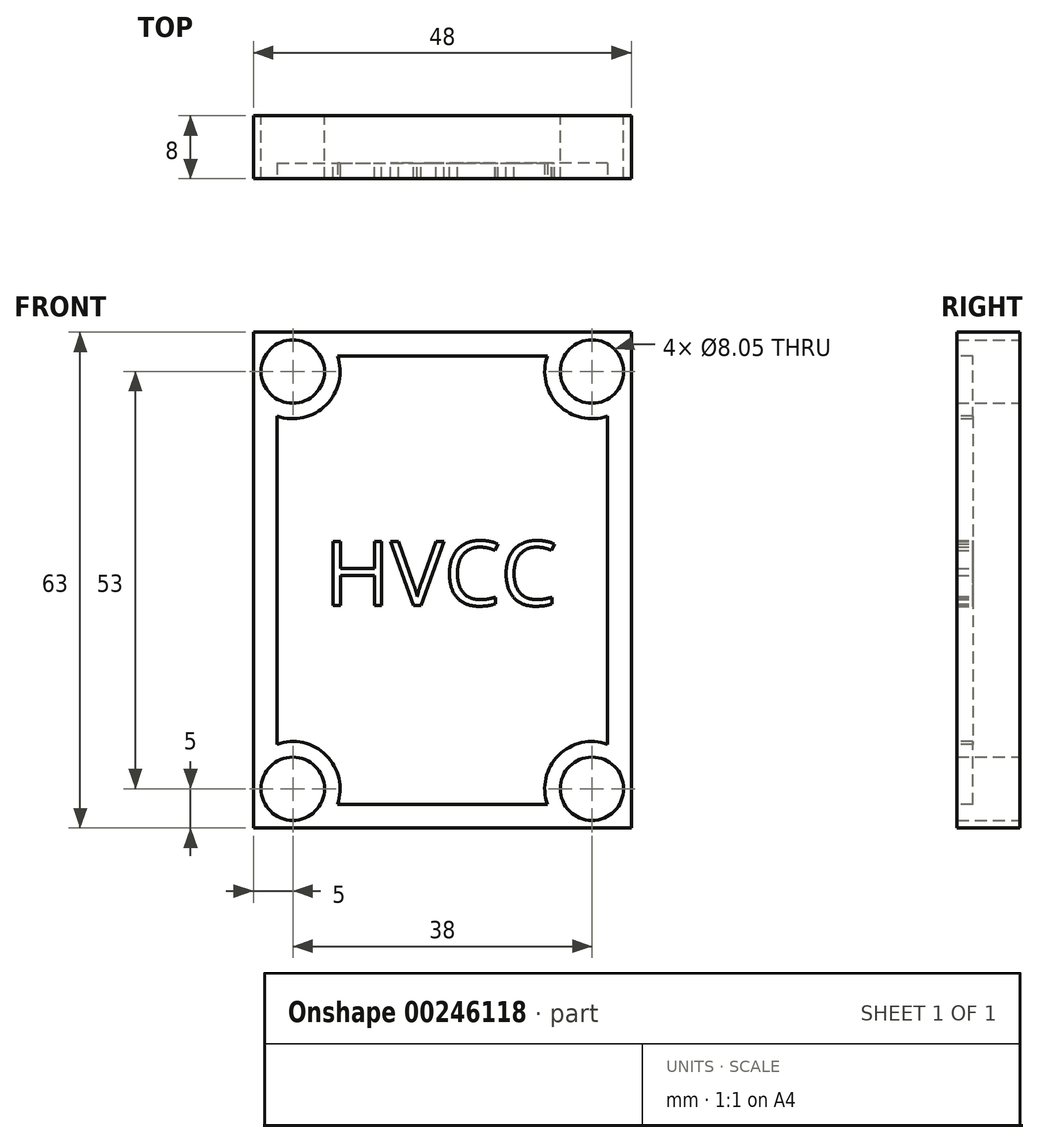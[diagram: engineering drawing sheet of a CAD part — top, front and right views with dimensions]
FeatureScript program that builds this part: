
annotation { "Feature Type Name" : "Feature", "Feature Type Description" : "" }
export const myFeature = defineFeature(function(context is Context, id is Id, definition is map)
    precondition{}
    {
        {
            var Q0;
            Q0=qCreatedBy(makeId("Front.planeOp"),FACE);
            var sketch = newSketch(context, id + "F0", { "sketchPlane" : qUnion([Q0])});
            skLineSegment(sketch, "E0.bottom", {"start": v(0, 0) * mm, "end": v(-48, 0) * mm});
            skLineSegment(sketch, "E0.top", {"start": v(0, -63) * mm, "end": v(-48, -63) * mm});
            skLineSegment(sketch, "E0.left", {"start": v(0, 0) * mm, "end": v(0, -63) * mm});
            skLineSegment(sketch, "E0.right", {"start": v(-48, 0) * mm, "end": v(-48, -63) * mm});
            skCircle(sketch, "E1", {"center": v(-43, -5) * mm, "radius": 4.03 * mm});
            skCircle(sketch, "E2", {"center": v(-5, -5) * mm, "radius": 4.03 * mm});
            skCircle(sketch, "E3", {"center": v(-43, -58) * mm, "radius": 4.03 * mm});
            skCircle(sketch, "E4", {"center": v(-5, -58) * mm, "radius": 4.03 * mm});
            skLineSegment(sketch, "E5", {"start": v(-45, -13) * mm, "end": v(-45, -50) * mm});
            skLineSegment(sketch, "E6", {"start": v(-43, -52) * mm, "end": v(-43, -52) * mm});
            skLineSegment(sketch, "E7", {"start": v(-37, -58) * mm, "end": v(-37, -58) * mm});
            skLineSegment(sketch, "E8", {"start": v(-35, -60) * mm, "end": v(-13, -60) * mm});
            skLineSegment(sketch, "E9", {"start": v(-11, -58) * mm, "end": v(-11, -58) * mm});
            skLineSegment(sketch, "E10", {"start": v(-5, -52) * mm, "end": v(-5, -52) * mm});
            skLineSegment(sketch, "E11", {"start": v(-3, -50) * mm, "end": v(-3, -13) * mm});
            skLineSegment(sketch, "E12", {"start": v(-5, -11) * mm, "end": v(-5, -11) * mm});
            skLineSegment(sketch, "E13", {"start": v(-11, -5) * mm, "end": v(-11, -5) * mm});
            skLineSegment(sketch, "E14", {"start": v(-13, -3) * mm, "end": v(-35, -3) * mm});
            skLineSegment(sketch, "E15", {"start": v(-37, -5) * mm, "end": v(-37, -5) * mm});
            skLineSegment(sketch, "E16", {"start": v(-43, -11) * mm, "end": v(-43, -11) * mm});
            skLineSegment(sketch, "E17", {"start": v(-24, 0) * mm, "end": v(-24, -63) * mm, "construction": true});
            skLineSegment(sketch, "E18", {"start": v(-48, -31.5) * mm, "end": v(0, -31.5) * mm, "construction": true});
            skPoint(sketch, "E19.visualSharp", {"position": v(-37, -11) * mm});
            skArc(sketch, "E20.filletArc", {"start": v(-43, -11) * mm, "mid": v(-38.76, -9.24) * mm, "end": v(-37, -5) * mm});
            skPoint(sketch, "E21.visualSharp", {"position": v(-37, -3) * mm});
            skArc(sketch, "E21.filletArc", {"start": v(-35, -3) * mm, "mid": v(-36.41, -3.59) * mm, "end": v(-37, -5) * mm});
            skPoint(sketch, "E22.visualSharp", {"position": v(-45, -11) * mm});
            skArc(sketch, "E22.filletArc", {"start": v(-43, -11) * mm, "mid": v(-44.41, -11.59) * mm, "end": v(-45, -13) * mm});
            skPoint(sketch, "E23.visualSharp", {"position": v(-11, -11) * mm});
            skArc(sketch, "E23.filletArc", {"start": v(-11, -5) * mm, "mid": v(-9.24, -9.24) * mm, "end": v(-5, -11) * mm});
            skPoint(sketch, "E24.visualSharp", {"position": v(-11, -52) * mm});
            skArc(sketch, "E24.filletArc", {"start": v(-5, -52) * mm, "mid": v(-9.24, -53.76) * mm, "end": v(-11, -58) * mm});
            skPoint(sketch, "E25.visualSharp", {"position": v(-37, -52) * mm});
            skArc(sketch, "E25.filletArc", {"start": v(-37, -58) * mm, "mid": v(-38.76, -53.76) * mm, "end": v(-43, -52) * mm});
            skPoint(sketch, "E26.visualSharp", {"position": v(-11, -3) * mm});
            skArc(sketch, "E26.filletArc", {"start": v(-11, -5) * mm, "mid": v(-11.59, -3.59) * mm, "end": v(-13, -3) * mm});
            skPoint(sketch, "E27.visualSharp", {"position": v(-3, -11) * mm});
            skArc(sketch, "E27.filletArc", {"start": v(-3, -13) * mm, "mid": v(-3.59, -11.59) * mm, "end": v(-5, -11) * mm});
            skPoint(sketch, "E28.visualSharp", {"position": v(-3, -52) * mm});
            skArc(sketch, "E28.filletArc", {"start": v(-5, -52) * mm, "mid": v(-3.59, -51.41) * mm, "end": v(-3, -50) * mm});
            skPoint(sketch, "E29.visualSharp", {"position": v(-11, -60) * mm});
            skArc(sketch, "E29.filletArc", {"start": v(-13, -60) * mm, "mid": v(-11.59, -59.41) * mm, "end": v(-11, -58) * mm});
            skPoint(sketch, "E30.visualSharp", {"position": v(-37, -60) * mm});
            skArc(sketch, "E30.filletArc", {"start": v(-37, -58) * mm, "mid": v(-36.41, -59.41) * mm, "end": v(-35, -60) * mm});
            skPoint(sketch, "E31.visualSharp", {"position": v(-45, -52) * mm});
            skArc(sketch, "E31.filletArc", {"start": v(-45, -50) * mm, "mid": v(-44.41, -51.41) * mm, "end": v(-43, -52) * mm});
            skText(sketch, "E32", { "text": "HVCC", "fontName": "OpenSans-Regular.ttf"});
            const initialGuessF0  = {"E32": [-0.039, -0.03471, 1, 0, 0.00821]};
            skSetInitialGuess(sketch, initialGuessF0);
            skSolve(sketch);
        }
        {
            var Q0;
            Q0=makeQuery(id+"F0.imprint","IMPRINT",FACE,{"disambiguationData":[TD([[makeQuery(id+"F0.imprint","IMPRINT",EDGE,{"derivedFrom":sQuery(id+"F0.wireOp",EDGE,"E32.sketch_text.stroke-0")}),-1.0]])]});
            var Q1;
            Q1=makeQuery(id+"F0.imprint","IMPRINT",FACE,{"disambiguationData":[TD([[makeQuery(id+"F0.imprint","IMPRINT",EDGE,{"derivedFrom":sQuery(id+"F0.wireOp",EDGE,"E32.sketch_text.stroke-12")}),-1.0]])]});
            var Q2;
            Q2=makeQuery(id+"F0.imprint","IMPRINT",FACE,{"disambiguationData":[TD([[makeQuery(id+"F0.imprint","IMPRINT",EDGE,{"derivedFrom":sQuery(id+"F0.wireOp",EDGE,"E32.sketch_text.stroke-21")}),-1.0]])]});
            var Q3;
            Q3=makeQuery(id+"F0.imprint","IMPRINT",FACE,{"disambiguationData":[TD([[makeQuery(id+"F0.imprint","IMPRINT",EDGE,{"derivedFrom":sQuery(id+"F0.wireOp",EDGE,"E32.sketch_text.stroke-36")}),-1.0]])]});
            var Q4;
            Q4=makeQuery(id+"F0.imprint","IMPRINT",FACE,{"disambiguationData":[TD([[makeQuery(id+"F0.imprint","IMPRINT",EDGE,{"derivedFrom":sQuery(id+"F0.wireOp",EDGE,"E5")}),1.0]])]});
            var Q5;
            Q5=makeQuery(id+"F0.imprint","IMPRINT",FACE,{"disambiguationData":[TD([[makeQuery(id+"F0.imprint","IMPRINT",EDGE,{"derivedFrom":sQuery(id+"F0.wireOp",EDGE,"E0.bottom")}),1.0]])]});
            extrude(context, id + "F1", {"entities" : qUnion([Q0, Q1, Q2, Q3, Q4, Q5]), "depth" : 8 * mm});
        }
        {
            var Q0;
            Q0=makeQuery(id+"F1.opExtrude","CAP_FACE",FACE,{"disambiguationData":[OSD([sQuery(id+"F0.wireOp",EDGE,"E0.bottom"),sQuery(id+"F0.wireOp",EDGE,"E0.top"),sQuery(id+"F0.wireOp",EDGE,"E0.left"),sQuery(id+"F0.wireOp",EDGE,"E0.right"),sQuery(id+"F0.wireOp",EDGE,"E1"),sQuery(id+"F0.wireOp",EDGE,"E2"),sQuery(id+"F0.wireOp",EDGE,"E3"),sQuery(id+"F0.wireOp",EDGE,"E4")])],"isStart":false});
            var sketch = newSketch(context, id + "F2", { "sketchPlane" : qUnion([Q0])});
            skArc(sketch, "E33.0", {"start": v(-45, -10.66) * mm, "mid": v(-38.76, -9.24) * mm, "end": v(-37.34, -3) * mm});
            skLineSegment(sketch, "E33.1", {"start": v(-10.66, -3) * mm, "end": v(-37.34, -3) * mm});
            skLineSegment(sketch, "E33.2", {"start": v(-45, -10.66) * mm, "end": v(-45, -52.34) * mm});
            skArc(sketch, "E33.3", {"start": v(-10.66, -3) * mm, "mid": v(-9.24, -9.24) * mm, "end": v(-3, -10.66) * mm});
            skArc(sketch, "E33.4", {"start": v(-37.34, -60) * mm, "mid": v(-38.76, -53.76) * mm, "end": v(-45, -52.34) * mm});
            skLineSegment(sketch, "E33.5", {"start": v(-37.34, -60) * mm, "end": v(-10.66, -60) * mm});
            skArc(sketch, "E33.6", {"start": v(-3, -52.34) * mm, "mid": v(-9.24, -53.76) * mm, "end": v(-10.66, -60) * mm});
            skLineSegment(sketch, "E33.7", {"start": v(-3, -52.34) * mm, "end": v(-3, -10.66) * mm});
            skSolve(sketch);
        }
        {
            var Q0;
            Q0 = qSketchRegion(id + "F2", true);
            extrude(context, id + "F3", {"entities" : qUnion([Q0]), "operationType" : NewBodyOperationType.REMOVE, "oppositeDirection" : true, "depth" : 2 * mm});
        }
        {
            var Q0;
            Q0=makeQuery(id+"F0.imprint","IMPRINT",FACE,{"disambiguationData":[TD([[makeQuery(id+"F0.imprint","IMPRINT",EDGE,{"derivedFrom":sQuery(id+"F0.wireOp",EDGE,"E32.sketch_text.stroke-36")}),-1.0]])]});
            var Q1;
            Q1=makeQuery(id+"F0.imprint","IMPRINT",FACE,{"disambiguationData":[TD([[makeQuery(id+"F0.imprint","IMPRINT",EDGE,{"derivedFrom":sQuery(id+"F0.wireOp",EDGE,"E32.sketch_text.stroke-21")}),-1.0]])]});
            var Q2;
            Q2=makeQuery(id+"F0.imprint","IMPRINT",FACE,{"disambiguationData":[TD([[makeQuery(id+"F0.imprint","IMPRINT",EDGE,{"derivedFrom":sQuery(id+"F0.wireOp",EDGE,"E32.sketch_text.stroke-12")}),-1.0]])]});
            var Q3;
            Q3=makeQuery(id+"F0.imprint","IMPRINT",FACE,{"disambiguationData":[TD([[makeQuery(id+"F0.imprint","IMPRINT",EDGE,{"derivedFrom":sQuery(id+"F0.wireOp",EDGE,"E32.sketch_text.stroke-0")}),-1.0]])]});
            extrude(context, id + "F4", {"entities" : qUnion([Q0, Q1, Q2, Q3]), "operationType" : NewBodyOperationType.ADD, "depth" : 8 * mm});
        }
    });
